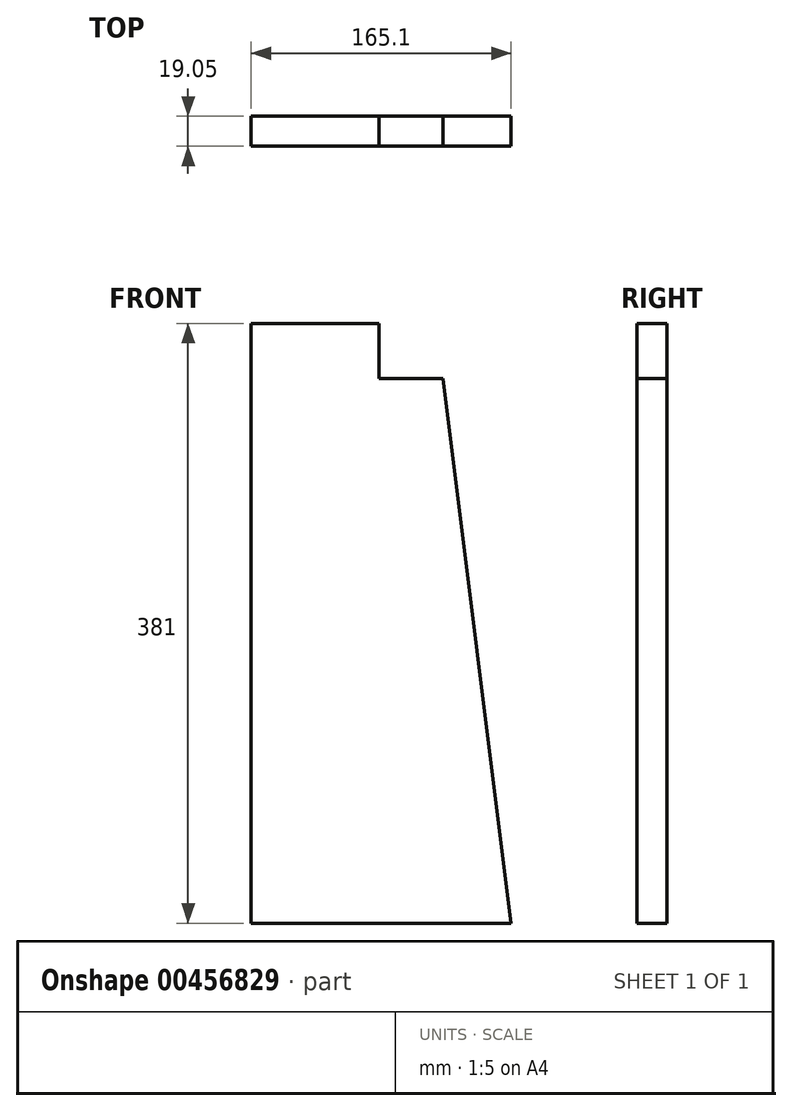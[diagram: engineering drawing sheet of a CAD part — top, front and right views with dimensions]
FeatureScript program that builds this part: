
annotation { "Feature Type Name" : "Feature", "Feature Type Description" : "" }
export const myFeature = defineFeature(function(context is Context, id is Id, definition is map)
    precondition{}
    {
        {
            var Q0;
            Q0=qCreatedBy(makeId("Front.planeOp"),FACE);
            var sketch = newSketch(context, id + "F0", { "sketchPlane" : qUnion([Q0])});
            skLineSegment(sketch, "E0", {"start": v(0, 272.95) * mm, "end": v(0, -133.45) * mm});
            skLineSegment(sketch, "E1", {"start": v(0, -133.45) * mm, "end": v(165.1, -133.45) * mm});
            skLineSegment(sketch, "E2", {"start": v(165.1, -133.45) * mm, "end": v(114.3, 272.95) * mm});
            skLineSegment(sketch, "E3", {"start": v(114.3, 272.95) * mm, "end": v(0, 272.95) * mm});
            skSolve(sketch);
        }
        {
            var Q0;
            Q0 = qSketchRegion(id + "F0", true);
            extrude(context, id + "F1", {"entities" : qUnion([Q0]), "oppositeDirection" : true, "depth" : 19.05 * mm});
        }
        {
            var Q0;
            Q0=makeQuery(id+"F1.opExtrude","CAP_FACE",FACE,{"disambiguationData":[OSD([sQuery(id+"F0.wireOp",EDGE,"E0"),sQuery(id+"F0.wireOp",EDGE,"E1"),sQuery(id+"F0.wireOp",EDGE,"E2"),sQuery(id+"F0.wireOp",EDGE,"E3")])],"isStart":true});
            var sketch = newSketch(context, id + "F2", { "sketchPlane" : qUnion([Q0])});
            skLineSegment(sketch, "E4", {"start": v(0, 247.55) * mm, "end": v(81.26, 247.55) * mm});
            skLineSegment(sketch, "E5", {"start": v(81.26, 247.55) * mm, "end": v(81.26, 212.63) * mm});
            skLineSegment(sketch, "E6", {"start": v(81.26, 212.63) * mm, "end": v(121.84, 212.63) * mm});
            skLineSegment(sketch, "E7", {"start": v(121.84, 212.63) * mm, "end": v(114.3, 272.95) * mm});
            skLineSegment(sketch, "E8", {"start": v(114.3, 272.95) * mm, "end": v(0, 272.95) * mm});
            skLineSegment(sketch, "E9", {"start": v(0, 272.95) * mm, "end": v(0, 247.55) * mm});
            skSolve(sketch);
        }
        {
            var Q0;
            Q0 = qSketchRegion(id + "F2", true);
            extrude(context, id + "F3", {"entities" : qUnion([Q0]), "operationType" : NewBodyOperationType.REMOVE, "endBound" : BoundingType.THROUGH_ALL, "oppositeDirection" : true, "depth" : 25.4 * mm});
        }
    });
